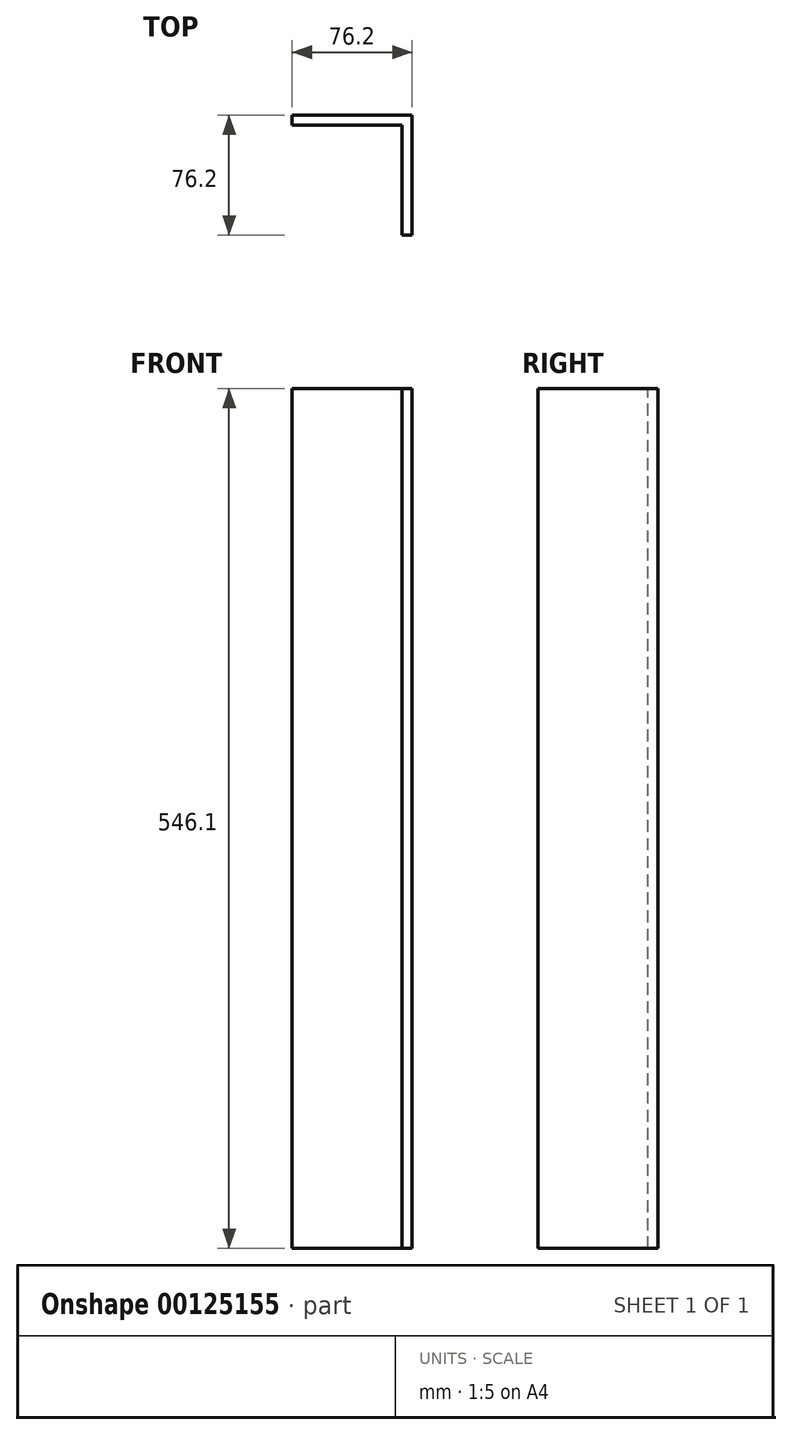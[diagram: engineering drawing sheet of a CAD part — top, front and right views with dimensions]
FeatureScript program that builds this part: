
annotation { "Feature Type Name" : "Feature", "Feature Type Description" : "" }
export const myFeature = defineFeature(function(context is Context, id is Id, definition is map)
    precondition{}
    {
        {
            var Q0;
            Q0=qCreatedBy(makeId("Top.planeOp"),FACE);
            var sketch = newSketch(context, id + "F0", { "sketchPlane" : qUnion([Q0])});
            skLineSegment(sketch, "E0", {"start": v(-76.2, 0) * mm, "end": v(0, 0) * mm});
            skLineSegment(sketch, "E1", {"start": v(0, 0) * mm, "end": v(0, -76.2) * mm});
            skLineSegment(sketch, "E2.0", {"start": v(-6.35, -6.35) * mm, "end": v(-6.35, -76.2) * mm});
            skLineSegment(sketch, "E2.1", {"start": v(-76.2, -6.35) * mm, "end": v(-6.35, -6.35) * mm});
            skLineSegment(sketch, "E3", {"start": v(-76.2, 0) * mm, "end": v(-76.2, -6.35) * mm});
            skLineSegment(sketch, "E4", {"start": v(-6.35, -76.2) * mm, "end": v(0, -76.2) * mm});
            skSolve(sketch);
        }
        {
            var Q0;
            Q0=qSketchRegion(id+"F0",true);
            extrude(context, id + "F1", {"entities" : qUnion([Q0]), "oppositeDirection" : true, "depth" : 546.1 * mm});
        }
    });
